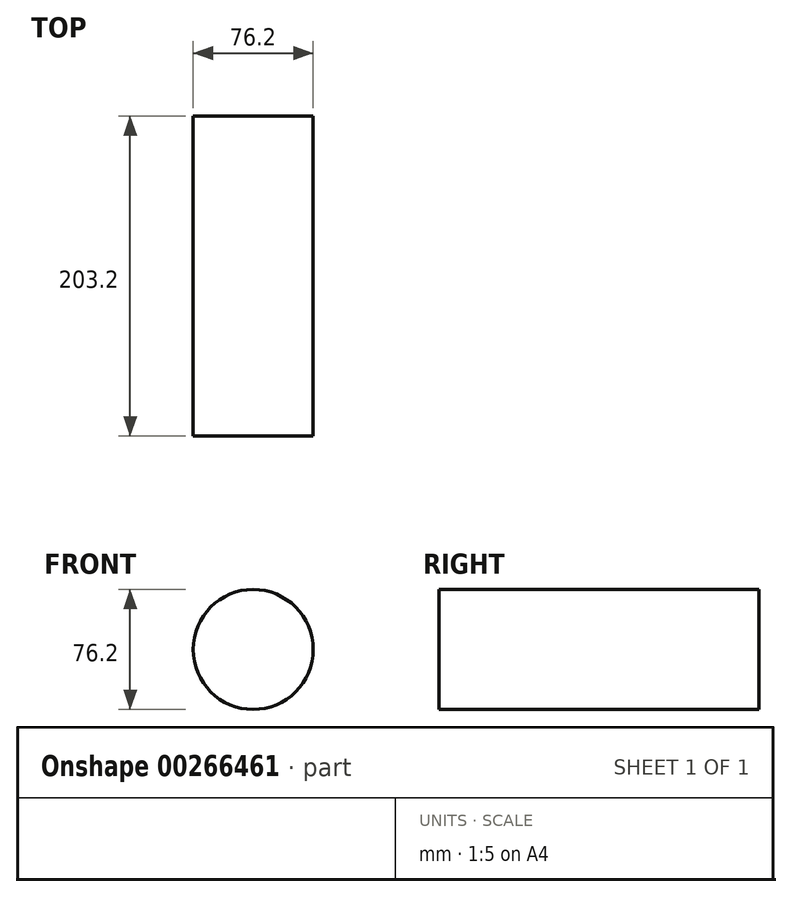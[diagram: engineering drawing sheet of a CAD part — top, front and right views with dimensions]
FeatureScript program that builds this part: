
annotation { "Feature Type Name" : "Feature", "Feature Type Description" : "" }
export const myFeature = defineFeature(function(context is Context, id is Id, definition is map)
    precondition{}
    {
        {
            var Q0;
            Q0=qCreatedBy(makeId("Front.planeOp"),FACE);
            var sketch = newSketch(context, id + "F0", { "sketchPlane" : qUnion([Q0])});
            skCircle(sketch, "E0", {"center": v(0, 0) * mm, "radius": 38.1 * mm});
            skSolve(sketch);
        }
        {
            var Q0;
            Q0 = qSketchRegion(id + "F0", true);
            extrude(context, id + "F1", {"entities" : qUnion([Q0]), "depth" : 203.2 * mm});
        }
    });
